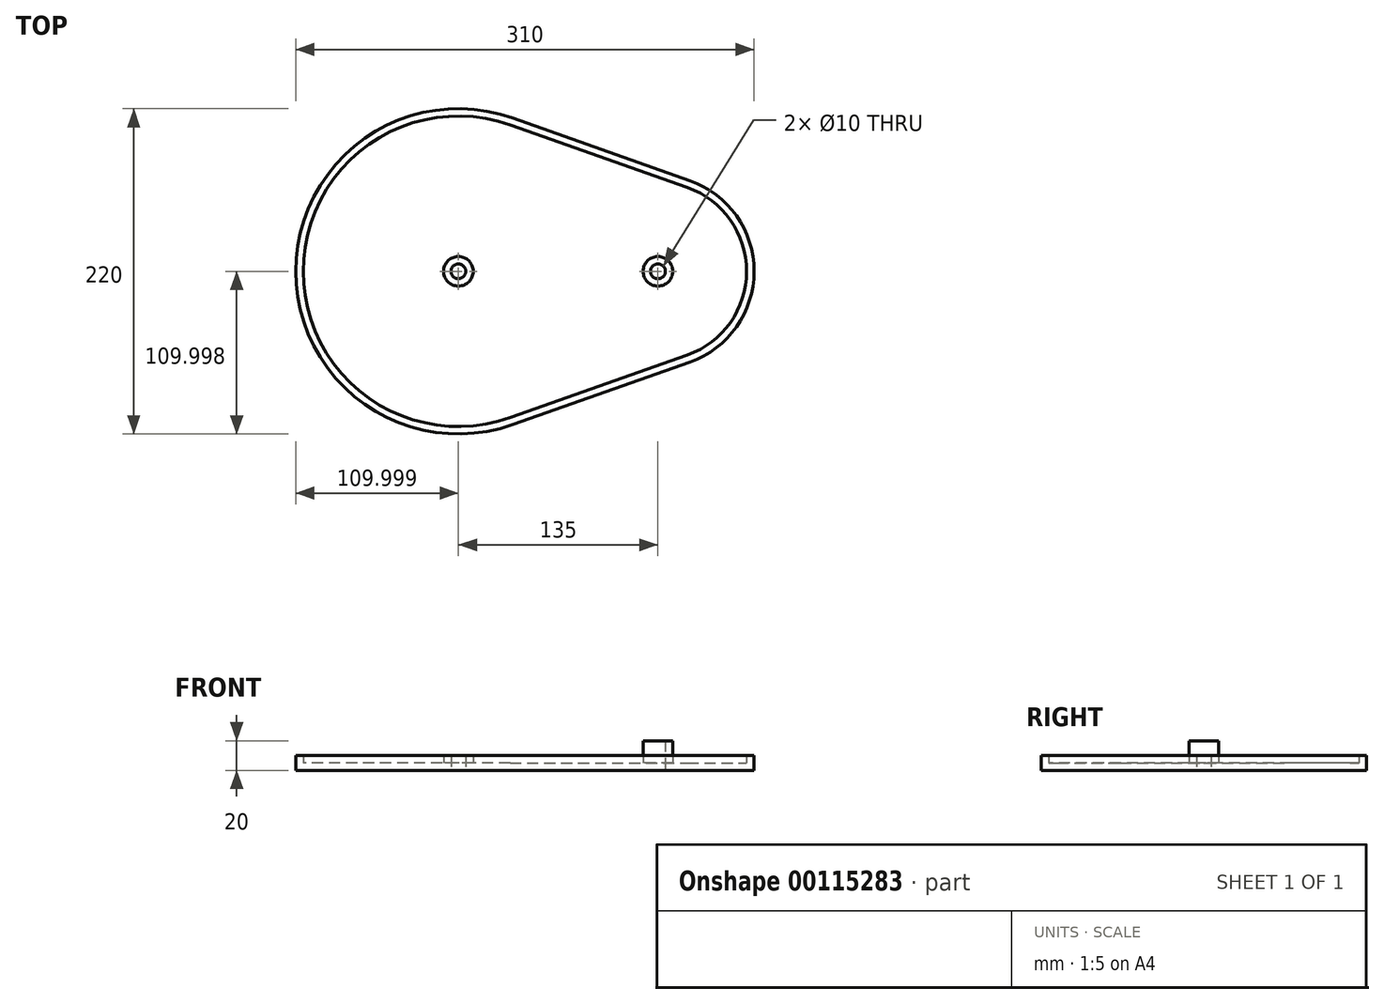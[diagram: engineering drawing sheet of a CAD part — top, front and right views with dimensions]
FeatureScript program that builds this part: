
annotation { "Feature Type Name" : "Feature", "Feature Type Description" : "" }
export const myFeature = defineFeature(function(context is Context, id is Id, definition is map)
    precondition{}
    {
        {
            var Q0;
            Q0=qCreatedBy(makeId("Top.planeOp"),FACE);
            var sketch = newSketch(context, id + "F0", { "sketchPlane" : qUnion([Q0])});
            skArc(sketch, "E0", {"start": v(42.39, -123.04) * mm, "mid": v(-104.28, -226.75) * mm, "end": v(42.39, -330.46) * mm});
            skArc(sketch, "E1", {"start": v(162.39, -288.04) * mm, "mid": v(205.72, -226.75) * mm, "end": v(162.39, -165.47) * mm});
            skCircle(sketch, "E2", {"center": v(5.72, -226.75) * mm, "radius": 5 * mm});
            skCircle(sketch, "E3", {"center": v(140.72, -226.75) * mm, "radius": 5 * mm});
            skLineSegment(sketch, "E4", {"start": v(42.39, -123.04) * mm, "end": v(162.39, -165.47) * mm});
            skLineSegment(sketch, "E5.MirrorCS", {"start": v(42.39, -330.46) * mm, "end": v(162.39, -288.04) * mm});
            skSolve(sketch);
        }
        {
            var Q0;
            Q0=makeQuery(id+"F0.imprint","IMPRINT",FACE,{"disambiguationData":[TD([[makeQuery(id+"F0.imprint","IMPRINT",EDGE,{"derivedFrom":sQuery(id+"F0.wireOp",EDGE,"E0")}),1.0]])]});
            extrude(context, id + "F1", {"entities" : qUnion([Q0]), "depth" : 10 * mm});
        }
        {
            var Q0;
            Q0=makeQuery(id+"F1.opExtrude","CAP_FACE",FACE,{"disambiguationData":[OSD([sQuery(id+"F0.wireOp",EDGE,"E0"),sQuery(id+"F0.wireOp",EDGE,"E1"),sQuery(id+"F0.wireOp",EDGE,"E2"),sQuery(id+"F0.wireOp",EDGE,"E3"),sQuery(id+"F0.wireOp",EDGE,"E4"),sQuery(id+"F0.wireOp",EDGE,"E5.MirrorCS")])],"isStart":false});
            shell(context, id + "F2", {"entities" : qUnion([Q0]), "thickness" : 5 * mm});
        }
        {
            var Q0;
            Q0=makeQuery(id+"F1.opExtrude","CAP_FACE",FACE,{"disambiguationData":[OSD([sQuery(id+"F0.wireOp",EDGE,"E0"),sQuery(id+"F0.wireOp",EDGE,"E1"),sQuery(id+"F0.wireOp",EDGE,"E2"),sQuery(id+"F0.wireOp",EDGE,"E3"),sQuery(id+"F0.wireOp",EDGE,"E4"),sQuery(id+"F0.wireOp",EDGE,"E5.MirrorCS")])],"isStart":false});
            extrude(context, id + "F3", {"entities" : qUnion([Q0]), "operationType" : NewBodyOperationType.ADD, "depth" : 10 * mm});
        }
    });
